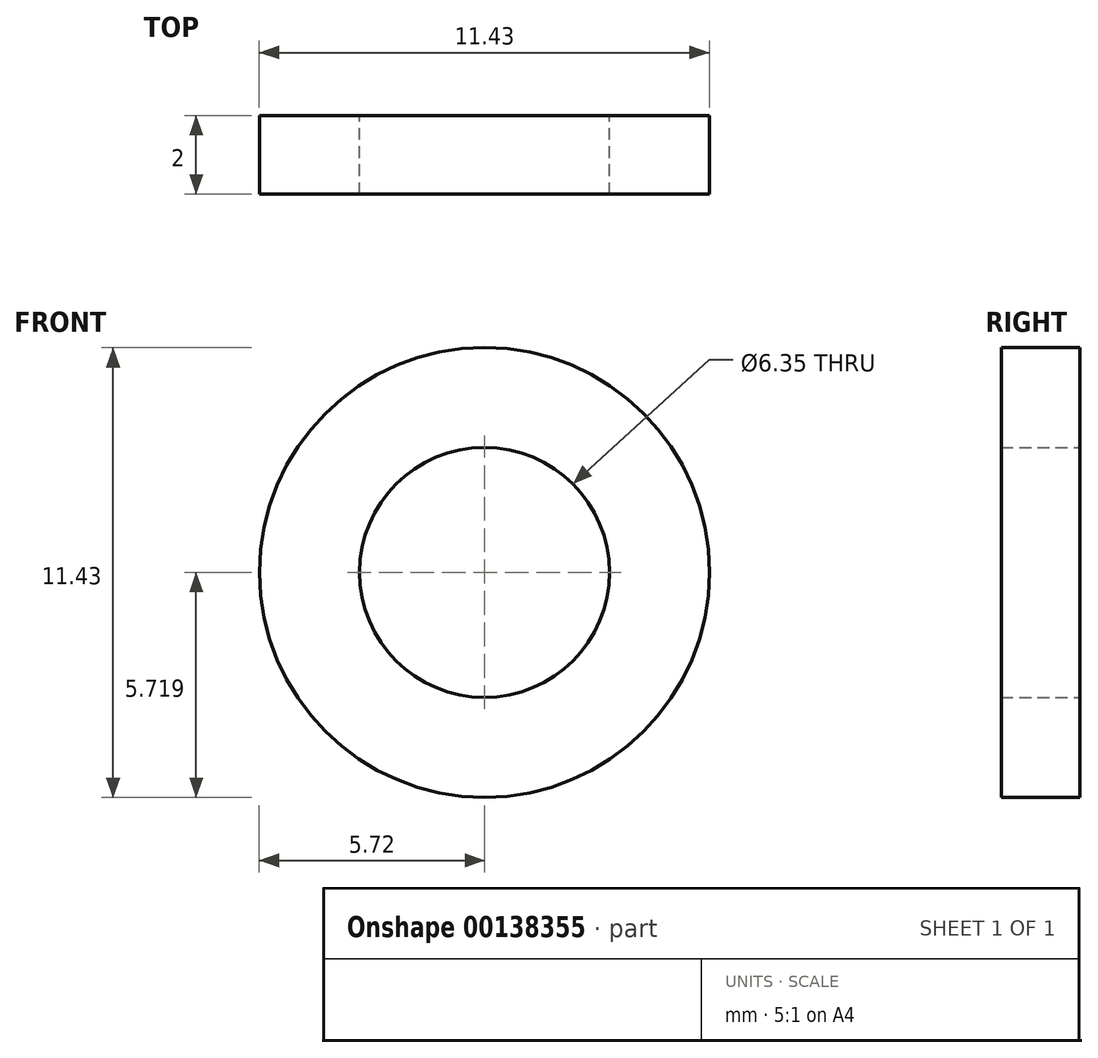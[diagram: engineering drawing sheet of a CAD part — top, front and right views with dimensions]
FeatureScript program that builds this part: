
annotation { "Feature Type Name" : "Feature", "Feature Type Description" : "" }
export const myFeature = defineFeature(function(context is Context, id is Id, definition is map)
    precondition{}
    {
        {
            var Q0;
            Q0=qCreatedBy(makeId("Front.planeOp"),FACE);
            var sketch = newSketch(context, id + "F0", { "sketchPlane" : qUnion([Q0])});
            skCircle(sketch, "E0", {"center": v(-20.78, 23.75) * mm, "radius": 3.18 * mm});
            skCircle(sketch, "E1", {"center": v(-20.78, 23.75) * mm, "radius": 5.72 * mm});
            skSolve(sketch);
        }
        {
            var Q0;
            Q0 = qSketchRegion(id + "F0", true);
            extrude(context, id + "F1", {"entities" : qUnion([Q0]), "depth" : 2 * mm});
        }
    });
